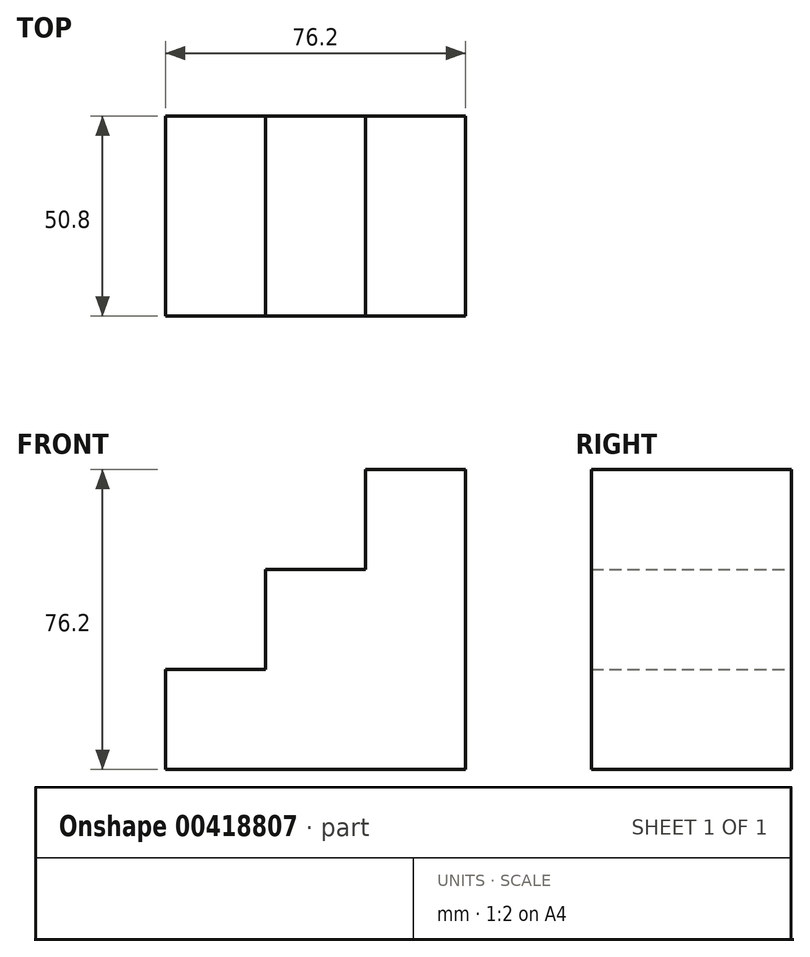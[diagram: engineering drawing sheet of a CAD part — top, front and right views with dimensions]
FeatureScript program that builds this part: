
annotation { "Feature Type Name" : "Feature", "Feature Type Description" : "" }
export const myFeature = defineFeature(function(context is Context, id is Id, definition is map)
    precondition{}
    {
        {
            var Q0;
            Q0=qCreatedBy(makeId("Front.planeOp"),FACE);
            var sketch = newSketch(context, id + "F0", { "sketchPlane" : qUnion([Q0])});
            skLineSegment(sketch, "E0", {"start": v(-76.2, 0) * mm, "end": v(0, 0) * mm});
            skLineSegment(sketch, "E1", {"start": v(0, 0) * mm, "end": v(0, 76.2) * mm});
            skLineSegment(sketch, "E2", {"start": v(0, 76.2) * mm, "end": v(-25.4, 76.2) * mm});
            skLineSegment(sketch, "E3", {"start": v(-25.4, 76.2) * mm, "end": v(-25.4, 50.8) * mm});
            skLineSegment(sketch, "E4", {"start": v(-25.4, 50.8) * mm, "end": v(-50.8, 50.8) * mm});
            skLineSegment(sketch, "E5", {"start": v(-50.8, 50.8) * mm, "end": v(-50.8, 25.4) * mm});
            skLineSegment(sketch, "E6", {"start": v(-50.8, 25.4) * mm, "end": v(-76.2, 25.4) * mm});
            skLineSegment(sketch, "E7", {"start": v(-76.2, 25.4) * mm, "end": v(-76.2, 0) * mm});
            skSolve(sketch);
        }
        {
            var Q0;
            Q0=makeQuery(id+"F0.imprint","IMPRINT",FACE,{"disambiguationData":[TD([[makeQuery(id+"F0.imprint","IMPRINT",EDGE,{"derivedFrom":sQuery(id+"F0.wireOp",EDGE,"E0")}),1.0]])]});
            extrude(context, id + "F1", {"entities" : qUnion([Q0]), "depth" : 50.8 * mm});
        }
    });
